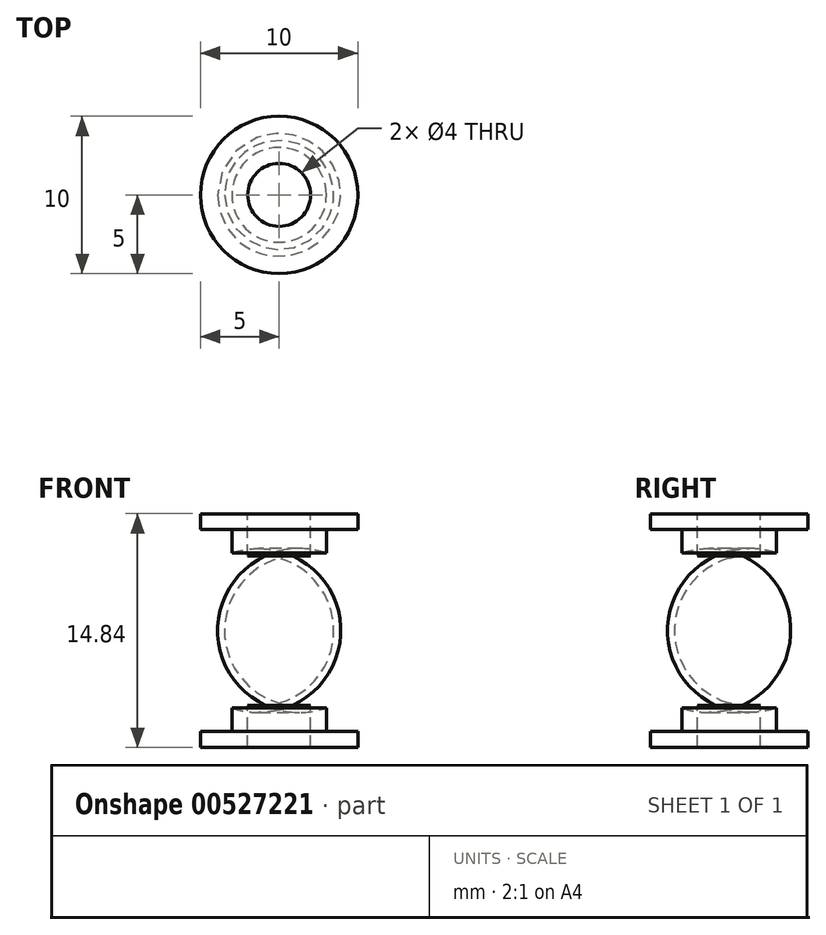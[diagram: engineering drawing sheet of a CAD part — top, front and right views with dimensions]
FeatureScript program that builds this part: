
annotation { "Feature Type Name" : "Feature", "Feature Type Description" : "" }
export const myFeature = defineFeature(function(context is Context, id is Id, definition is map)
    precondition{}
    {
        {
            var Q0;
            Q0=qCreatedBy(makeId("Front.planeOp"),FACE);
            var sketch = newSketch(context, id + "F0", { "sketchPlane" : qUnion([Q0])});
            skLineSegment(sketch, "E0", {"start": v(-3, 4.92) * mm, "end": v(-3, 6.42) * mm});
            skLineSegment(sketch, "E1", {"start": v(-3, 6.42) * mm, "end": v(-5, 6.42) * mm});
            skLineSegment(sketch, "E2", {"start": v(-5, 6.42) * mm, "end": v(-5, 7.42) * mm});
            skLineSegment(sketch, "E3", {"start": v(-5, 7.42) * mm, "end": v(-2, 7.42) * mm});
            skLineSegment(sketch, "E4.MirrorCS", {"start": v(-3, -4.92) * mm, "end": v(-3, -6.42) * mm});
            skLineSegment(sketch, "E5.MirrorCS", {"start": v(-5, -7.42) * mm, "end": v(-2, -7.42) * mm});
            skLineSegment(sketch, "E6.MirrorCS", {"start": v(-3, -6.42) * mm, "end": v(-5, -6.42) * mm});
            skLineSegment(sketch, "E7.MirrorCS", {"start": v(-5, -6.42) * mm, "end": v(-5, -7.42) * mm});
            skLineSegment(sketch, "E8", {"start": v(0, 11.09) * mm, "end": v(0, -11.16) * mm, "construction": true});
            skArc(sketch, "E9", {"start": v(-3, 4.92) * mm, "mid": v(-6.5, 0) * mm, "end": v(-3, -4.92) * mm});
            skPoint(sketch, "E10.center.orphan", {"position": v(-2, 0) * mm});
            skArc(sketch, "E11", {"start": v(-2, 4.73) * mm, "mid": v(-6.1, 0) * mm, "end": v(-2, -4.74) * mm});
            skLineSegment(sketch, "E12", {"start": v(-2, -7.42) * mm, "end": v(-2, -4.74) * mm});
            skLineSegment(sketch, "E13", {"start": v(-2, 4.73) * mm, "end": v(-2, 7.42) * mm});
            skSolve(sketch);
        }
        {
            var Q0;
            Q0 = qSketchRegion(id + "F0", true);
            var Q1;
            Q1=sQuery(id+"F0.wireOp",EDGE,"E8");
            revolve(context, id + "F1", {"entities" : qUnion([Q0]), "axis" : qUnion([Q1]), "revolveType" : RevolveType.FULL});
        }
    });
